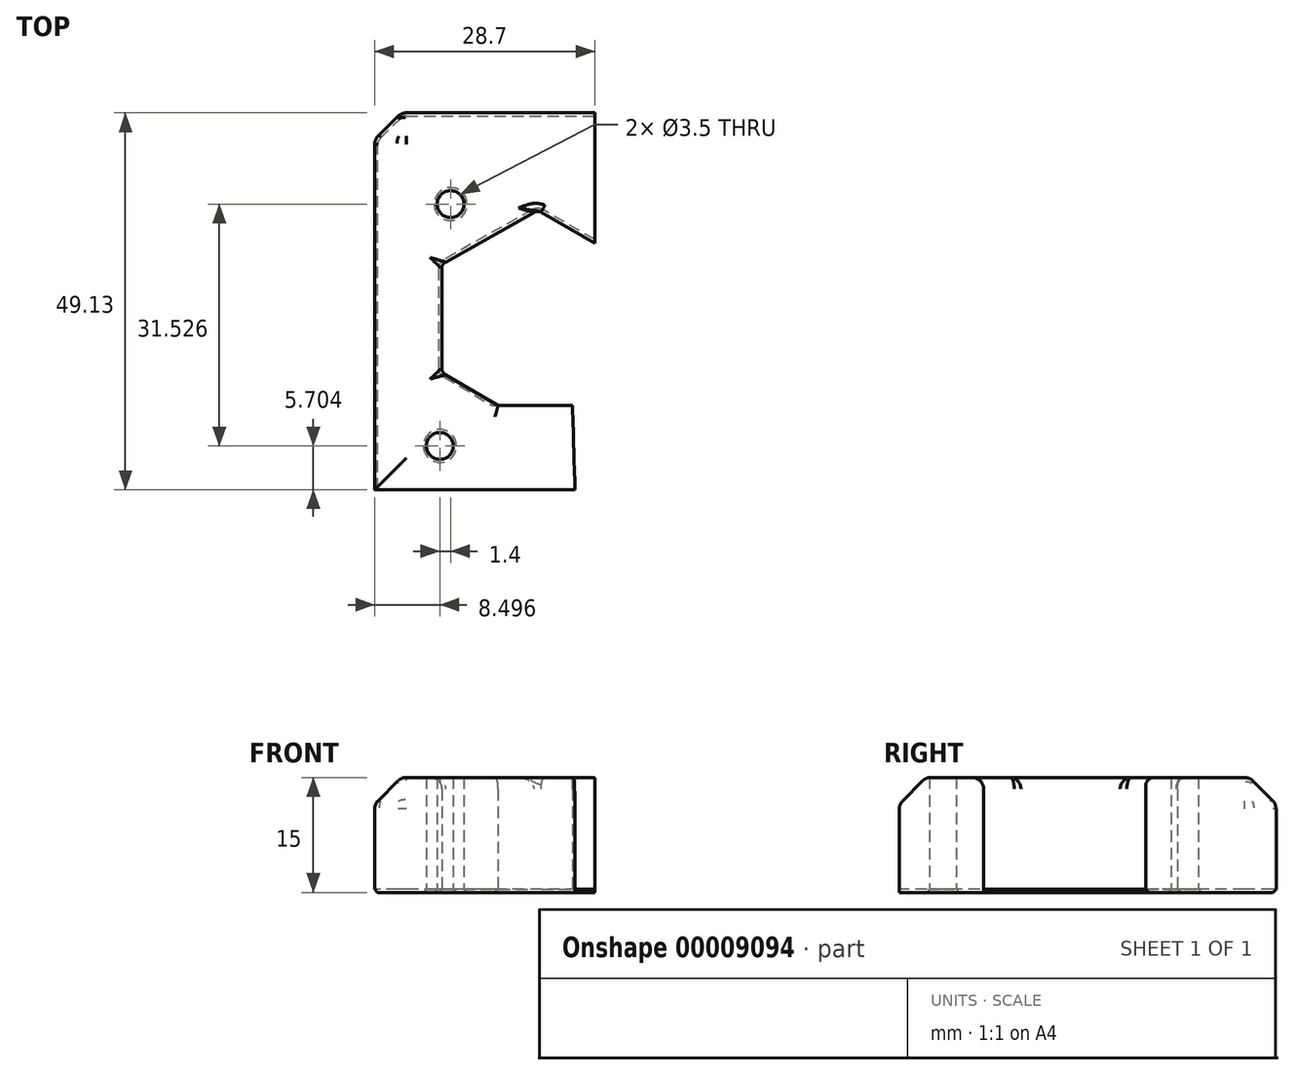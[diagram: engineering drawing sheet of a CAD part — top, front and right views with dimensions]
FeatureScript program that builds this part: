
annotation { "Feature Type Name" : "Feature", "Feature Type Description" : "" }
export const myFeature = defineFeature(function(context is Context, id is Id, definition is map)
    precondition{}
    {
        {
            var Q0;
            Q0=qCreatedBy(makeId("Top.planeOp"),FACE);
            var sketch = newSketch(context, id + "F0", { "sketchPlane" : qUnion([Q0])});
            skLineSegment(sketch, "E0.top", {"start": v(-24.31, -15.29) * mm, "end": v(-8.21, -15.29) * mm});
            skLineSegment(sketch, "E0.left", {"start": v(-24.31, 33.84) * mm, "end": v(-24.31, -15.29) * mm});
            skLineSegment(sketch, "E1", {"start": v(-24.31, 14.1) * mm, "end": v(-15.57, 14.1) * mm});
            skLineSegment(sketch, "E2", {"start": v(-15.57, 14.1) * mm, "end": v(-15.57, 0) * mm});
            skLineSegment(sketch, "E3.top", {"start": v(-24.31, -4.29) * mm, "end": v(-8.21, -4.29) * mm});
            skLineSegment(sketch, "E3.left", {"start": v(-24.31, -15.29) * mm, "end": v(-24.31, -4.29) * mm});
            skLineSegment(sketch, "E3.right", {"start": v(-8.21, -15.29) * mm, "end": v(-8.21, -4.29) * mm});
            skLineSegment(sketch, "E4", {"start": v(-15.57, 0) * mm, "end": v(-8.21, -4.29) * mm});
            skLineSegment(sketch, "E5", {"start": v(-15.57, 14.1) * mm, "end": v(-3.07, 21.14) * mm});
            skLineSegment(sketch, "E6", {"start": v(-3.07, 21.14) * mm, "end": v(-3.07, 33.84) * mm});
            skLineSegment(sketch, "E7", {"start": v(-3.07, 21.14) * mm, "end": v(0.94, 18.84) * mm});
            skLineSegment(sketch, "E8", {"start": v(0.94, 18.84) * mm, "end": v(0.94, 33.84) * mm});
            skLineSegment(sketch, "E9", {"start": v(-8.21, -15.29) * mm, "end": v(1.79, -15.29) * mm});
            skLineSegment(sketch, "E10", {"start": v(1.79, -15.29) * mm, "end": v(-8.21, -4.29) * mm});
            skLineSegment(sketch, "E11", {"start": v(-24.31, 33.84) * mm, "end": v(0.94, 33.84) * mm});
            skLineSegment(sketch, "E12", {"start": v(-8.21, -4.29) * mm, "end": v(1.47, -4.29) * mm});
            skLineSegment(sketch, "E13", {"start": v(1.47, -4.29) * mm, "end": v(1.79, -15.29) * mm});
            skLineSegment(sketch, "E14", {"start": v(0.94, 33.84) * mm, "end": v(4.39, 33.84) * mm});
            skLineSegment(sketch, "E15", {"start": v(4.39, 33.84) * mm, "end": v(4.39, 16.86) * mm});
            skLineSegment(sketch, "E16", {"start": v(4.39, 16.86) * mm, "end": v(0.94, 18.84) * mm});
            skCircle(sketch, "E17", {"center": v(-14.41, 21.94) * mm, "radius": 1.75 * mm});
            skCircle(sketch, "E18", {"center": v(-15.81, -9.59) * mm, "radius": 1.75 * mm});
            skLineSegment(sketch, "E19", {"start": v(-14.41, 21.94) * mm, "end": v(-24.31, 21.94) * mm});
            skLineSegment(sketch, "E20", {"start": v(-14.41, 21.94) * mm, "end": v(-14.41, 33.84) * mm});
            skLineSegment(sketch, "E21", {"start": v(-15.81, -9.59) * mm, "end": v(-15.81, -15.29) * mm});
            skLineSegment(sketch, "E22", {"start": v(-15.81, -9.59) * mm, "end": v(-24.31, -9.59) * mm});
            skSolve(sketch);
        }
        {
            var Q0;
            Q0 = qSketchRegion(id + "F0", true);
            extrude(context, id + "F1", {"entities" : qUnion([Q0]), "depth" : 15 * mm});
        }
        {
            var Q0;
            Q0=makeQuery(id+"F1.opExtrude","CAP_EDGE",EDGE,{"disambiguationData":[OSD([sQuery(id+"F0.wireOp",EDGE,"E0.bottom"),sQuery(id+"F0.wireOp",EDGE,"5d418e40-5359-4053-b136-f79983218c00")])],"isStart":false});
            var Q1;
            Q1=makeQuery(id+"F1.opExtrude","CAP_EDGE",EDGE,{"disambiguationData":[OSD([sQuery(id+"F0.wireOp",EDGE,"E2")])],"isStart":false});
            var Q2;
            Q2=makeQuery(id+"F1.opExtrude","CAP_EDGE",EDGE,{"disambiguationData":[OSD([sQuery(id+"F0.wireOp",EDGE,"E5")])],"isStart":false});
            var Q3;
            Q3=makeQuery(id+"F1.opExtrude","CAP_EDGE",EDGE,{"disambiguationData":[OSD([sQuery(id+"F0.wireOp",EDGE,"E4")])],"isStart":false});
            var Q4;
            Q4=makeQuery(id+"F1.opExtrude","CAP_EDGE",EDGE,{"disambiguationData":[OSD([sQuery(id+"F0.wireOp",EDGE,"02881490-eef5-47a4-9113-f653e2ad7d51")])],"isStart":false});
            var Q5;
            Q5=makeQuery(id+"F1.opExtrude","CAP_EDGE",EDGE,{"disambiguationData":[OSD([sQuery(id+"F0.wireOp",EDGE,"6d11c3b7-84e3-41b8-aeba-338aa3b88252")])],"isStart":false});
            var Q6;
            Q6=makeQuery(id+"F1.opExtrude","CAP_EDGE",EDGE,{"disambiguationData":[OSD([sQuery(id+"F0.wireOp",EDGE,"a9e62e1d-703b-49f6-ae14-db8655108b4f")])],"isStart":false});
            var Q7;
            Q7=makeQuery(id+"F1.opExtrude","CAP_EDGE",EDGE,{"disambiguationData":[OSD([sQuery(id+"F0.wireOp",EDGE,"8eba5e31-6d4f-494a-8465-a316eab055b9")])],"isStart":false});
            var Q8;
            Q8=makeQuery(id+"F1.opExtrude","CAP_EDGE",EDGE,{"disambiguationData":[OSD([sQuery(id+"F0.wireOp",EDGE,"055a8850-a2ce-43db-9250-46ca403b5d6c")])],"isStart":false});
            var Q9;
            Q9=makeQuery(id+"F1.opExtrude","CAP_EDGE",EDGE,{"disambiguationData":[OSD([sQuery(id+"F0.wireOp",EDGE,"E12")])],"isStart":false});
            fillet(context, id + "F2", {"entities" : qUnion([Q0, Q1, Q2, Q3, Q4, Q5, Q6, Q7, Q8, Q9]), "radius" : 1.5 * mm, "tangentPropagation" : true, "allowEdgeOverflow" : false});
        }
        {
            var Q0;
            Q0=makeQuery(id+"F1.opExtrude","SWEPT_EDGE",EDGE,{"disambiguationData":[OSD([sQuery(id+"F0.wireOp",EDGE,"E5"),sQuery(id+"F0.wireOp",EDGE,"E6"),sQuery(id+"F0.wireOp",EDGE,"E7")])]});
            var Q1;
            Q1=makeQuery(id+"F1.opExtrude","SWEPT_EDGE",EDGE,{"disambiguationData":[OSD([sQuery(id+"F0.wireOp",EDGE,"E1"),sQuery(id+"F0.wireOp",EDGE,"e06c5d60-8db6-466d-9d73-d0a4a5ec3b6d"),sQuery(id+"F0.wireOp",EDGE,"E2"),sQuery(id+"F0.wireOp",EDGE,"E5")])]});
            var Q2;
            Q2=makeQuery(id+"F1.opExtrude","CAP_EDGE",EDGE,{"disambiguationData":[OSD([sQuery(id+"F0.wireOp",EDGE,"E7")])],"isStart":false});
            var Q3;
            Q3=makeQuery(id+"F1.opExtrude","SWEPT_EDGE",EDGE,{"disambiguationData":[OSD([sQuery(id+"F0.wireOp",EDGE,"E2"),sQuery(id+"F0.wireOp",EDGE,"E4")])]});
            fillet(context, id + "F3", {"entities" : qUnion([Q0, Q1, Q2, Q3]), "radius" : 1 * mm, "tangentPropagation" : true, "allowEdgeOverflow" : false});
        }
        {
            var Q0;
            Q0=makeQuery(id+"F1.opExtrude","CAP_EDGE",EDGE,{"disambiguationData":[OSD([sQuery(id+"F0.wireOp",EDGE,"E0.top"),sQuery(id+"F0.wireOp",EDGE,"E9")])],"isStart":false});
            var Q1;
            Q1=makeQuery(id+"F1.opExtrude","CAP_EDGE",EDGE,{"disambiguationData":[OSD([sQuery(id+"F0.wireOp",EDGE,"E0.left"),sQuery(id+"F0.wireOp",EDGE,"E3.left")])],"isStart":false});
            var Q2;
            Q2=makeQuery(id+"F1.opExtrude","CAP_EDGE",EDGE,{"disambiguationData":[OSD([sQuery(id+"F0.wireOp",EDGE,"E11"),sQuery(id+"F0.wireOp",EDGE,"E14")])],"isStart":false});
            var Q3;
            Q3=makeQuery(id+"F1.opExtrude","SWEPT_EDGE",EDGE,{"disambiguationData":[OSD([sQuery(id+"F0.wireOp",EDGE,"E0.top"),sQuery(id+"F0.wireOp",EDGE,"E3.left")])]});
            var Q4;
            Q4=makeQuery(id+"F1.opExtrude","SWEPT_EDGE",EDGE,{"disambiguationData":[OSD([sQuery(id+"F0.wireOp",EDGE,"E0.left"),sQuery(id+"F0.wireOp",EDGE,"E11")])]});
            chamfer(context, id + "F4", {"entities" : qUnion([Q0, Q1, Q2, Q3, Q4]), "width" : 3.5 * mm, "tangentPropagation" : true});
        }
        {
            var Q0;
            {var subQ0=sQuery(id+"F0.wireOp",EDGE,"E0.top");var subQ1=sQuery(id+"F0.wireOp",EDGE,"E9");Q0=makeQuery(id+"F4.opChamfer","BLEND_EDGE",EDGE,{"blendedFrom":[makeQuery(id+"F1.opExtrude","CAP_EDGE",EDGE,{"disambiguationData":[OSD([subQ0,subQ1])],"isStart":false}),makeQuery(id+"F1.opExtrude","CAP_FACE",FACE,{"disambiguationData":[OSD([sQuery(id+"F0.wireOp",EDGE,"E0.left"),sQuery(id+"F0.wireOp",EDGE,"E2"),subQ0,sQuery(id+"F0.wireOp",EDGE,"E3.left"),sQuery(id+"F0.wireOp",EDGE,"E4"),sQuery(id+"F0.wireOp",EDGE,"E5"),sQuery(id+"F0.wireOp",EDGE,"E7"),subQ1,sQuery(id+"F0.wireOp",EDGE,"E11"),sQuery(id+"F0.wireOp",EDGE,"E12"),sQuery(id+"F0.wireOp",EDGE,"E13"),sQuery(id+"F0.wireOp",EDGE,"E14"),sQuery(id+"F0.wireOp",EDGE,"E15"),sQuery(id+"F0.wireOp",EDGE,"E16"),sQuery(id+"F0.wireOp",EDGE,"E17"),sQuery(id+"F0.wireOp",EDGE,"E18")])],"isStart":false})],"blendedInto":[makeQuery(id+"F1.opExtrude","CAP_FACE",FACE,{"disambiguationData":[OSD([sQuery(id+"F0.wireOp",EDGE,"E0.left"),sQuery(id+"F0.wireOp",EDGE,"E2"),subQ0,sQuery(id+"F0.wireOp",EDGE,"E3.left"),sQuery(id+"F0.wireOp",EDGE,"E4"),sQuery(id+"F0.wireOp",EDGE,"E5"),sQuery(id+"F0.wireOp",EDGE,"E7"),subQ1,sQuery(id+"F0.wireOp",EDGE,"E11"),sQuery(id+"F0.wireOp",EDGE,"E12"),sQuery(id+"F0.wireOp",EDGE,"E13"),sQuery(id+"F0.wireOp",EDGE,"E14"),sQuery(id+"F0.wireOp",EDGE,"E15"),sQuery(id+"F0.wireOp",EDGE,"E16"),sQuery(id+"F0.wireOp",EDGE,"E17"),sQuery(id+"F0.wireOp",EDGE,"E18")])],"isStart":false})]});}
            var Q1;
            {var subQ0=sQuery(id+"F0.wireOp",EDGE,"E0.left");var subQ1=sQuery(id+"F0.wireOp",EDGE,"E3.left");Q1=makeQuery(id+"F4.opChamfer","BLEND_EDGE",EDGE,{"blendedFrom":[makeQuery(id+"F1.opExtrude","CAP_EDGE",EDGE,{"disambiguationData":[OSD([subQ0,subQ1])],"isStart":false}),makeQuery(id+"F1.opExtrude","CAP_FACE",FACE,{"disambiguationData":[OSD([subQ0,sQuery(id+"F0.wireOp",EDGE,"E2"),sQuery(id+"F0.wireOp",EDGE,"E0.top"),subQ1,sQuery(id+"F0.wireOp",EDGE,"E4"),sQuery(id+"F0.wireOp",EDGE,"E5"),sQuery(id+"F0.wireOp",EDGE,"E7"),sQuery(id+"F0.wireOp",EDGE,"E9"),sQuery(id+"F0.wireOp",EDGE,"E11"),sQuery(id+"F0.wireOp",EDGE,"E12"),sQuery(id+"F0.wireOp",EDGE,"E13"),sQuery(id+"F0.wireOp",EDGE,"E14"),sQuery(id+"F0.wireOp",EDGE,"E15"),sQuery(id+"F0.wireOp",EDGE,"E16"),sQuery(id+"F0.wireOp",EDGE,"E17"),sQuery(id+"F0.wireOp",EDGE,"E18")])],"isStart":false})],"blendedInto":[makeQuery(id+"F1.opExtrude","CAP_FACE",FACE,{"disambiguationData":[OSD([subQ0,sQuery(id+"F0.wireOp",EDGE,"E2"),sQuery(id+"F0.wireOp",EDGE,"E0.top"),subQ1,sQuery(id+"F0.wireOp",EDGE,"E4"),sQuery(id+"F0.wireOp",EDGE,"E5"),sQuery(id+"F0.wireOp",EDGE,"E7"),sQuery(id+"F0.wireOp",EDGE,"E9"),sQuery(id+"F0.wireOp",EDGE,"E11"),sQuery(id+"F0.wireOp",EDGE,"E12"),sQuery(id+"F0.wireOp",EDGE,"E13"),sQuery(id+"F0.wireOp",EDGE,"E14"),sQuery(id+"F0.wireOp",EDGE,"E15"),sQuery(id+"F0.wireOp",EDGE,"E16"),sQuery(id+"F0.wireOp",EDGE,"E17"),sQuery(id+"F0.wireOp",EDGE,"E18")])],"isStart":false})]});}
            var Q2;
            {var subQ0=sQuery(id+"F0.wireOp",EDGE,"E0.top");var subQ1=sQuery(id+"F0.wireOp",EDGE,"E9");Q2=makeQuery(id+"F4.opChamfer","BLEND_EDGE",EDGE,{"blendedFrom":[makeQuery(id+"F1.opExtrude","CAP_EDGE",EDGE,{"disambiguationData":[OSD([subQ0,subQ1])],"isStart":false}),makeQuery(id+"F1.opExtrude","SWEPT_FACE",FACE,{"disambiguationData":[OSD([subQ0,subQ1])]})],"blendedInto":[makeQuery(id+"F1.opExtrude","SWEPT_FACE",FACE,{"disambiguationData":[OSD([subQ0,subQ1])]})]});}
            var Q3;
            {var subQ0=sQuery(id+"F0.wireOp",EDGE,"E0.left");var subQ1=sQuery(id+"F0.wireOp",EDGE,"E3.left");Q3=makeQuery(id+"F4.opChamfer","BLEND_EDGE",EDGE,{"blendedFrom":[makeQuery(id+"F1.opExtrude","CAP_EDGE",EDGE,{"disambiguationData":[OSD([subQ0,subQ1])],"isStart":false}),makeQuery(id+"F1.opExtrude","SWEPT_FACE",FACE,{"disambiguationData":[OSD([subQ0,subQ1])]})],"blendedInto":[makeQuery(id+"F1.opExtrude","SWEPT_FACE",FACE,{"disambiguationData":[OSD([subQ0,subQ1])]})]});}
            var Q4;
            {var subQ0=sQuery(id+"F0.wireOp",EDGE,"E3.left");Q4=makeQuery(id+"F4.opChamfer","BLEND_EDGE",EDGE,{"blendedFrom":[makeQuery(id+"F1.opExtrude","CAP_VERTEX",VERTEX,{"disambiguationData":[OSD([sQuery(id+"F0.wireOp",EDGE,"E0.top"),subQ0])],"isStart":false}),makeQuery(id+"F1.opExtrude","CAP_EDGE",EDGE,{"disambiguationData":[OSD([sQuery(id+"F0.wireOp",EDGE,"E0.left"),subQ0])],"isStart":false})],"blendedInto":[]});}
            var Q5;
            {var subQ0=sQuery(id+"F0.wireOp",EDGE,"E0.top");Q5=makeQuery(id+"F4.opChamfer","BLEND_EDGE",EDGE,{"blendedFrom":[makeQuery(id+"F1.opExtrude","CAP_VERTEX",VERTEX,{"disambiguationData":[OSD([subQ0,sQuery(id+"F0.wireOp",EDGE,"E3.left")])],"isStart":false}),makeQuery(id+"F1.opExtrude","CAP_EDGE",EDGE,{"disambiguationData":[OSD([subQ0,sQuery(id+"F0.wireOp",EDGE,"E9")])],"isStart":false})],"blendedInto":[]});}
            var Q6;
            {var subQ0=sQuery(id+"F0.wireOp",EDGE,"E0.top");var subQ1=sQuery(id+"F0.wireOp",EDGE,"E3.left");Q6=makeQuery(id+"F4.opChamfer","BLEND_EDGE",EDGE,{"blendedFrom":[makeQuery(id+"F1.opExtrude","CAP_VERTEX",VERTEX,{"disambiguationData":[OSD([subQ0,subQ1])],"isStart":false}),makeQuery(id+"F1.opExtrude","SWEPT_EDGE",EDGE,{"disambiguationData":[OSD([subQ0,subQ1])]})],"blendedInto":[]});}
            var Q7;
            {var subQ0=sQuery(id+"F0.wireOp",EDGE,"E3.left");Q7=makeQuery(id+"F4.opChamfer","BLEND_EDGE",EDGE,{"blendedFrom":[makeQuery(id+"F1.opExtrude","SWEPT_EDGE",EDGE,{"disambiguationData":[OSD([sQuery(id+"F0.wireOp",EDGE,"E0.top"),subQ0])]}),makeQuery(id+"F1.opExtrude","SWEPT_FACE",FACE,{"disambiguationData":[OSD([sQuery(id+"F0.wireOp",EDGE,"E0.left"),subQ0])]})],"blendedInto":[makeQuery(id+"F1.opExtrude","SWEPT_FACE",FACE,{"disambiguationData":[OSD([sQuery(id+"F0.wireOp",EDGE,"E0.left"),subQ0])]})]});}
            var Q8;
            {var subQ0=sQuery(id+"F0.wireOp",EDGE,"E0.top");Q8=makeQuery(id+"F4.opChamfer","BLEND_EDGE",EDGE,{"blendedFrom":[makeQuery(id+"F1.opExtrude","SWEPT_EDGE",EDGE,{"disambiguationData":[OSD([subQ0,sQuery(id+"F0.wireOp",EDGE,"E3.left")])]}),makeQuery(id+"F1.opExtrude","SWEPT_FACE",FACE,{"disambiguationData":[OSD([subQ0,sQuery(id+"F0.wireOp",EDGE,"E9")])]})],"blendedInto":[makeQuery(id+"F1.opExtrude","SWEPT_FACE",FACE,{"disambiguationData":[OSD([subQ0,sQuery(id+"F0.wireOp",EDGE,"E9")])]})]});}
            var Q9;
            {var subQ0=sQuery(id+"F0.wireOp",EDGE,"E0.left");Q9=makeQuery(id+"F4.opChamfer","BLEND_EDGE",EDGE,{"blendedFrom":[makeQuery(id+"F1.opExtrude","CAP_VERTEX",VERTEX,{"disambiguationData":[OSD([subQ0,sQuery(id+"F0.wireOp",EDGE,"E11")])],"isStart":false}),makeQuery(id+"F1.opExtrude","CAP_EDGE",EDGE,{"disambiguationData":[OSD([subQ0,sQuery(id+"F0.wireOp",EDGE,"E3.left")])],"isStart":false})],"blendedInto":[]});}
            var Q10;
            {var subQ0=sQuery(id+"F0.wireOp",EDGE,"E11");Q10=makeQuery(id+"F4.opChamfer","BLEND_EDGE",EDGE,{"blendedFrom":[makeQuery(id+"F1.opExtrude","CAP_VERTEX",VERTEX,{"disambiguationData":[OSD([sQuery(id+"F0.wireOp",EDGE,"E0.left"),subQ0])],"isStart":false}),makeQuery(id+"F1.opExtrude","CAP_EDGE",EDGE,{"disambiguationData":[OSD([subQ0,sQuery(id+"F0.wireOp",EDGE,"E14")])],"isStart":false})],"blendedInto":[]});}
            var Q11;
            {var subQ0=sQuery(id+"F0.wireOp",EDGE,"E0.left");var subQ1=sQuery(id+"F0.wireOp",EDGE,"E11");Q11=makeQuery(id+"F4.opChamfer","BLEND_EDGE",EDGE,{"blendedFrom":[makeQuery(id+"F1.opExtrude","CAP_VERTEX",VERTEX,{"disambiguationData":[OSD([subQ0,subQ1])],"isStart":false}),makeQuery(id+"F1.opExtrude","SWEPT_EDGE",EDGE,{"disambiguationData":[OSD([subQ0,subQ1])]})],"blendedInto":[]});}
            var Q12;
            {var subQ0=sQuery(id+"F0.wireOp",EDGE,"E0.left");Q12=makeQuery(id+"F4.opChamfer","BLEND_EDGE",EDGE,{"blendedFrom":[makeQuery(id+"F1.opExtrude","SWEPT_EDGE",EDGE,{"disambiguationData":[OSD([subQ0,sQuery(id+"F0.wireOp",EDGE,"E11")])]}),makeQuery(id+"F1.opExtrude","SWEPT_FACE",FACE,{"disambiguationData":[OSD([subQ0,sQuery(id+"F0.wireOp",EDGE,"E3.left")])]})],"blendedInto":[makeQuery(id+"F1.opExtrude","SWEPT_FACE",FACE,{"disambiguationData":[OSD([subQ0,sQuery(id+"F0.wireOp",EDGE,"E3.left")])]})]});}
            var Q13;
            {var subQ0=sQuery(id+"F0.wireOp",EDGE,"E11");Q13=makeQuery(id+"F4.opChamfer","BLEND_EDGE",EDGE,{"blendedFrom":[makeQuery(id+"F1.opExtrude","SWEPT_EDGE",EDGE,{"disambiguationData":[OSD([sQuery(id+"F0.wireOp",EDGE,"E0.left"),subQ0])]}),makeQuery(id+"F1.opExtrude","SWEPT_FACE",FACE,{"disambiguationData":[OSD([subQ0,sQuery(id+"F0.wireOp",EDGE,"E14")])]})],"blendedInto":[makeQuery(id+"F1.opExtrude","SWEPT_FACE",FACE,{"disambiguationData":[OSD([subQ0,sQuery(id+"F0.wireOp",EDGE,"E14")])]})]});}
            var Q14;
            {var subQ0=sQuery(id+"F0.wireOp",EDGE,"E11");var subQ1=sQuery(id+"F0.wireOp",EDGE,"E14");Q14=makeQuery(id+"F4.opChamfer","BLEND_EDGE",EDGE,{"blendedFrom":[makeQuery(id+"F1.opExtrude","CAP_EDGE",EDGE,{"disambiguationData":[OSD([subQ0,subQ1])],"isStart":false}),makeQuery(id+"F1.opExtrude","SWEPT_FACE",FACE,{"disambiguationData":[OSD([subQ0,subQ1])]})],"blendedInto":[makeQuery(id+"F1.opExtrude","SWEPT_FACE",FACE,{"disambiguationData":[OSD([subQ0,subQ1])]})]});}
            var Q15;
            {var subQ0=sQuery(id+"F0.wireOp",EDGE,"E11");var subQ1=sQuery(id+"F0.wireOp",EDGE,"E14");Q15=makeQuery(id+"F4.opChamfer","BLEND_EDGE",EDGE,{"blendedFrom":[makeQuery(id+"F1.opExtrude","CAP_EDGE",EDGE,{"disambiguationData":[OSD([subQ0,subQ1])],"isStart":false}),makeQuery(id+"F1.opExtrude","CAP_FACE",FACE,{"disambiguationData":[OSD([sQuery(id+"F0.wireOp",EDGE,"E0.left"),sQuery(id+"F0.wireOp",EDGE,"E2"),sQuery(id+"F0.wireOp",EDGE,"E0.top"),sQuery(id+"F0.wireOp",EDGE,"E3.left"),sQuery(id+"F0.wireOp",EDGE,"E4"),sQuery(id+"F0.wireOp",EDGE,"E5"),sQuery(id+"F0.wireOp",EDGE,"E7"),sQuery(id+"F0.wireOp",EDGE,"E9"),subQ0,sQuery(id+"F0.wireOp",EDGE,"E12"),sQuery(id+"F0.wireOp",EDGE,"E13"),subQ1,sQuery(id+"F0.wireOp",EDGE,"E15"),sQuery(id+"F0.wireOp",EDGE,"E16"),sQuery(id+"F0.wireOp",EDGE,"E17"),sQuery(id+"F0.wireOp",EDGE,"E18")])],"isStart":false})],"blendedInto":[makeQuery(id+"F1.opExtrude","CAP_FACE",FACE,{"disambiguationData":[OSD([sQuery(id+"F0.wireOp",EDGE,"E0.left"),sQuery(id+"F0.wireOp",EDGE,"E2"),sQuery(id+"F0.wireOp",EDGE,"E0.top"),sQuery(id+"F0.wireOp",EDGE,"E3.left"),sQuery(id+"F0.wireOp",EDGE,"E4"),sQuery(id+"F0.wireOp",EDGE,"E5"),sQuery(id+"F0.wireOp",EDGE,"E7"),sQuery(id+"F0.wireOp",EDGE,"E9"),subQ0,sQuery(id+"F0.wireOp",EDGE,"E12"),sQuery(id+"F0.wireOp",EDGE,"E13"),subQ1,sQuery(id+"F0.wireOp",EDGE,"E15"),sQuery(id+"F0.wireOp",EDGE,"E16"),sQuery(id+"F0.wireOp",EDGE,"E17"),sQuery(id+"F0.wireOp",EDGE,"E18")])],"isStart":false})]});}
            fillet(context, id + "F5", {"entities" : qUnion([Q0, Q1, Q2, Q3, Q4, Q5, Q6, Q7, Q8, Q9, Q10, Q11, Q12, Q13, Q14, Q15]), "radius" : 1.5 * mm, "tangentPropagation" : true, "allowEdgeOverflow" : false});
        }
        {
            var Q0;
            Q0=makeQuery(id+"F1.opExtrude","CAP_EDGE",EDGE,{"disambiguationData":[OSD([sQuery(id+"F0.wireOp",EDGE,"E0.left"),sQuery(id+"F0.wireOp",EDGE,"E3.left")])],"isStart":true});
            var Q1;
            Q1=makeQuery(id+"F1.opExtrude","CAP_EDGE",EDGE,{"disambiguationData":[OSD([sQuery(id+"F0.wireOp",EDGE,"E2")])],"isStart":true});
            var Q2;
            Q2=makeQuery(id+"F1.opExtrude","CAP_EDGE",EDGE,{"disambiguationData":[OSD([sQuery(id+"F0.wireOp",EDGE,"E18")])],"isStart":true});
            var Q3;
            Q3=makeQuery(id+"F1.opExtrude","CAP_EDGE",EDGE,{"disambiguationData":[OSD([sQuery(id+"F0.wireOp",EDGE,"E17")])],"isStart":true});
            chamfer(context, id + "F6", {"entities" : qUnion([Q0, Q1, Q2, Q3]), "width" : .4 * mm, "tangentPropagation" : true});
        }
    });
